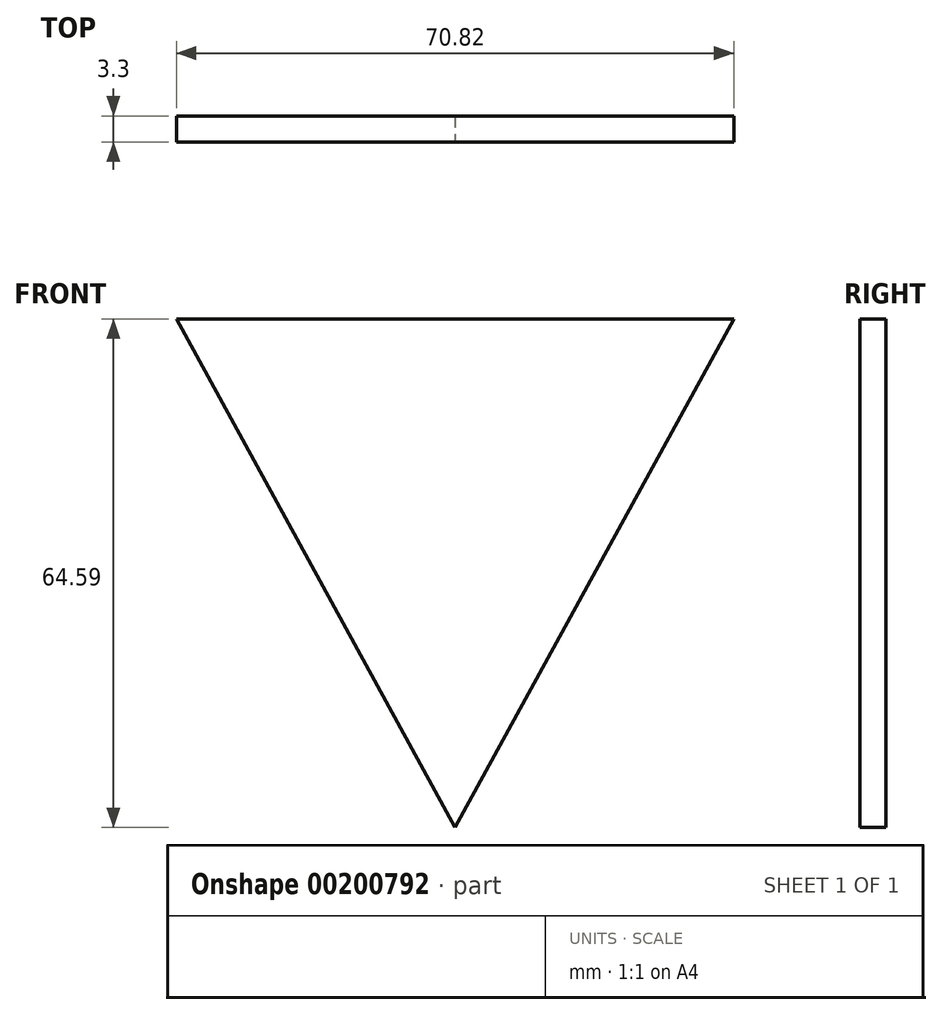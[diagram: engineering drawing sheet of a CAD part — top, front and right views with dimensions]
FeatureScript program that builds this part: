
annotation { "Feature Type Name" : "Feature", "Feature Type Description" : "" }
export const myFeature = defineFeature(function(context is Context, id is Id, definition is map)
    precondition{}
    {
        {
            var Q0;
            Q0=qCreatedBy(makeId("Front.planeOp"),FACE);
            var sketch = newSketch(context, id + "F0", { "sketchPlane" : qUnion([Q0])});
            skLineSegment(sketch, "E0", {"start": v(-35.4, 30.43) * mm, "end": v(35.4, 30.43) * mm});
            skLineSegment(sketch, "E1", {"start": v(35.4, 30.43) * mm, "end": v(0, -34.16) * mm});
            skLineSegment(sketch, "E2", {"start": v(0, -34.16) * mm, "end": v(-35.4, 30.43) * mm});
            skSolve(sketch);
        }
        {
            var Q0;
            Q0=makeQuery(id+"F0.imprint","IMPRINT",FACE,{"disambiguationData":[TD([[makeQuery(id+"F0.imprint","IMPRINT",EDGE,{"derivedFrom":sQuery(id+"F0.wireOp",EDGE,"E0")}),-1.0]])]});
            extrude(context, id + "F1", {"entities" : qUnion([Q0]), "oppositeDirection" : true, "depth" : 3.3 * mm});
        }
    });
